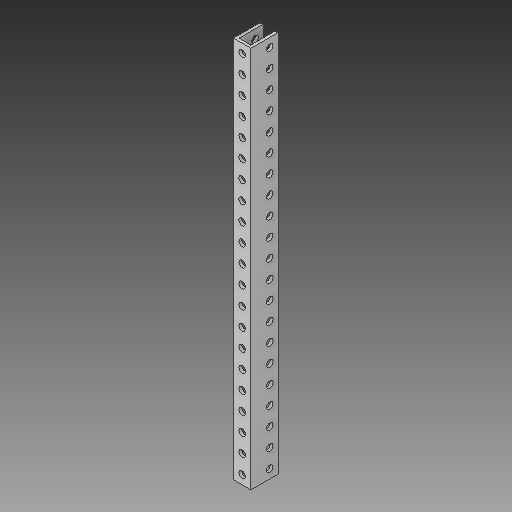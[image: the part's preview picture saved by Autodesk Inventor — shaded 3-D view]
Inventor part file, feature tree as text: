
AUTODESK INVENTOR PART (.ipt)
format: ipt  version: 2019 (Build 230136000, 136)  size: 168,960 bytes
history: native  units: in
note: dims shown in document units (in); Inventor stores cm internally (conversion verified against a paired STEP export)
features: fillet x1
ambient origin geometry x8: Origin, YZ Plane, XZ Plane, XY Plane, X Axis, Y Axis, Z Axis, Center Point
bodies: Solid1 (feature_tree)
feature tree (1):
  fillet  "Fillet1"  [1 undecoded]
note: 1 required parameter value undecoded (feature->parameter linkage not recoverable at this tier; creation-order binding heuristic only, values carry confidence <= 0.55)
